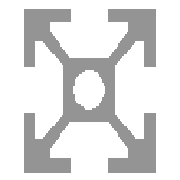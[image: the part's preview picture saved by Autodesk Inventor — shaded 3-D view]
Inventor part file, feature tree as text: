
AUTODESK INVENTOR PART (.ipt)
format: ipt  version: 2024 (Build 280153000, 153)  size: 227,840 bytes
history: native  units: in
note: dims shown in document units (in); Inventor stores cm internally (conversion verified against a paired STEP export)
features: other x26, extrude x1, fillet x1
ambient origin geometry x8: Origin, YZ Plane, XZ Plane, XY Plane, X Axis, Y Axis, Z Axis, Center Point
bodies: Body1 (feature_tree)
feature tree (28):
  other  "Table"
  other  "20x20 Channel-10"
  other  "20x20 Channel-20"
  other  "20x20 Channel-30"
  other  "20x20 Channel-40"
  other  "20x20 Channel-50"
  other  "20x20 Channel-100"
  other  "20x20 Channel-150"
  other  "20x20 Channel-200"
  other  "20x20 Channel-250"
  other  "20x20 Channel-300"
  other  "20x20 Channel-350"
  other  "20x20 Channel-400"
  other  "20x20 Channel-450"
  other  "20x20 Channel-500"
  other  "20x20 Channel-550"
  other  "20x20 Channel-560"
  other  "20x20 Channel-570"
  other  "20x20 Channel-580"
  other  "20x20 Channel-590"
  other  "20x20 Channel-600"
  other  "20x20 Channel-610"
  other  "20x20 Channel-620"
  other  "20x20 Channel-630"
  other  "20x20 Channel-640"
  other  "20x20 Channel-650"
  extrude  "Extrusion3"  Depth=0.7874in
  fillet  "Fillet2"  Radius=0.7874in
